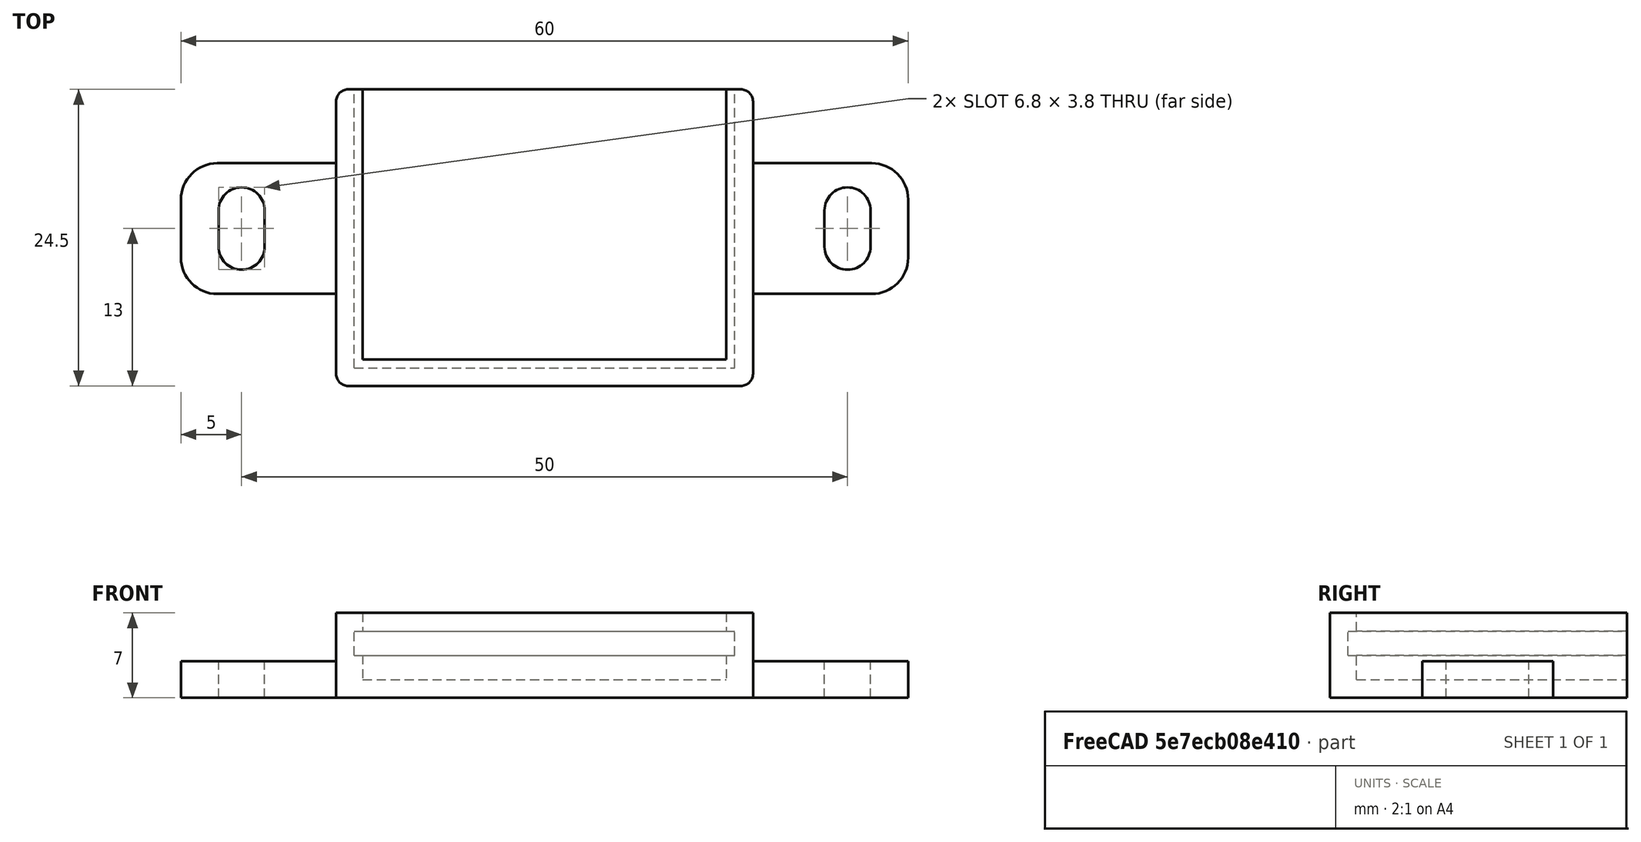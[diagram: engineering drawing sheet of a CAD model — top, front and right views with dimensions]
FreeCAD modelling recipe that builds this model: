
FCSTD DOCUMENT  (FreeCAD 0.18.4R)
Label: mpr121
License: FreeArt
LicenseURL: http://artlibre.org/licence/lal
objects: Part::Box×3, Part::MultiFuse×2, Spreadsheet::Sheet×1, Part::Fillet×1, Part::Feature×1, Part::Cut×1, App::Part×1
note: 8 computed .brp shape members not serialized (recipe doc carries the construction recipe); baked Part::Feature solids carry a one-line shape summary decoded from their .brp

FEATURE [Spreadsheet::Sheet] Spreadsheet  label="p"
  cells = A1=pcb_x; B1(pcb_x)=31.4; A2=pcb_y; B2(pcb_y)=23; A3=pcb_z; B3(pcb_z)=2; A4=pcb_under; B4(pcb_under)=2; A5=side_wall; B5(side_wall)=1.5; A6=pcb_side_lane; B6(pcb_side_lane)=0.7; A7=bottom_wall; B7(bottom_wall)=1.5; A8=pcb_above; B8(pcb_above)=1.5
FEATURE [Part::Box] Box  label="external cube"
  AttacherType = Attacher::AttachEngine3D
  Height = 7
  Length = 34.4
  Width = 24.5
  expr: Height = p.bottom_wall + p.pcb_under + p.pcb_z + p.pcb_above
  expr: Width = p.pcb_y + p.side_wall
  expr: Length = p.pcb_x + 2 * p.side_wall
FEATURE [Part::Box] Box006  label="internal cube"
  AttacherType = Attacher::AttachEngine3D
  Height = 5.5
  Length = 30
  Placement = pos=(2.2,2.2,1.5) rot=(0,0,1;0rad)
  Width = 23.1
  expr: Placement.Base.y = p.side_wall + p.pcb_side_lane
  expr: Placement.Base.x = p.side_wall + p.pcb_side_lane
  expr: Placement.Base.z = p.bottom_wall
  expr: Height = p.pcb_under + p.pcb_z + p.pcb_above
  expr: Width = p.pcb_y - 2 * p.pcb_side_lane + p.side_wall
  expr: Length = p.pcb_x - 2 * p.pcb_side_lane
FEATURE [Part::Box] Box007  label="pcb extract cube"
  AttacherType = Attacher::AttachEngine3D
  Height = 2
  Length = 31.4
  Placement = pos=(1.5,1.5,3.5) rot=(0,0,1;0rad)
  Width = 23
  expr: Placement.Base.y = p.side_wall
  expr: Placement.Base.x = p.side_wall
  expr: Length = p.pcb_x
  expr: Width = p.pcb_y
  expr: Placement.Base.z = p.bottom_wall + p.pcb_under
  expr: Height = p.pcb_z
FEATURE [Part::MultiFuse] Fusion  label="extract fusion"
  Shapes = -> [Box006,Box007]
FEATURE [Part::Fillet] Fillet  label="external fillet"
  Base = -> Box
  Edges = 4 edges r=1: [Edge1,Edge3,Edge5,Edge7]
FEATURE [Part::Feature] Cut003002  label="attach plane x dir002"
  shape: bbox 60 x 10.8 x 3 mm, 18 faces (baked)
FEATURE [Part::MultiFuse] Fusion001  label="mpr21 fusion"
  Shapes = -> [Fillet,Cut003002]
FEATURE [Part::Cut] Cut  label="mpr121 cut"
  Base = -> Fusion001
  Tool = -> Fusion
FEATURE [App::Part] Part  label="mpr121 pcb box part"
  Group = -> [Box,Fillet,Fusion001,Fusion,Box007,Box006,Cut]
  Origin = -> Origin
